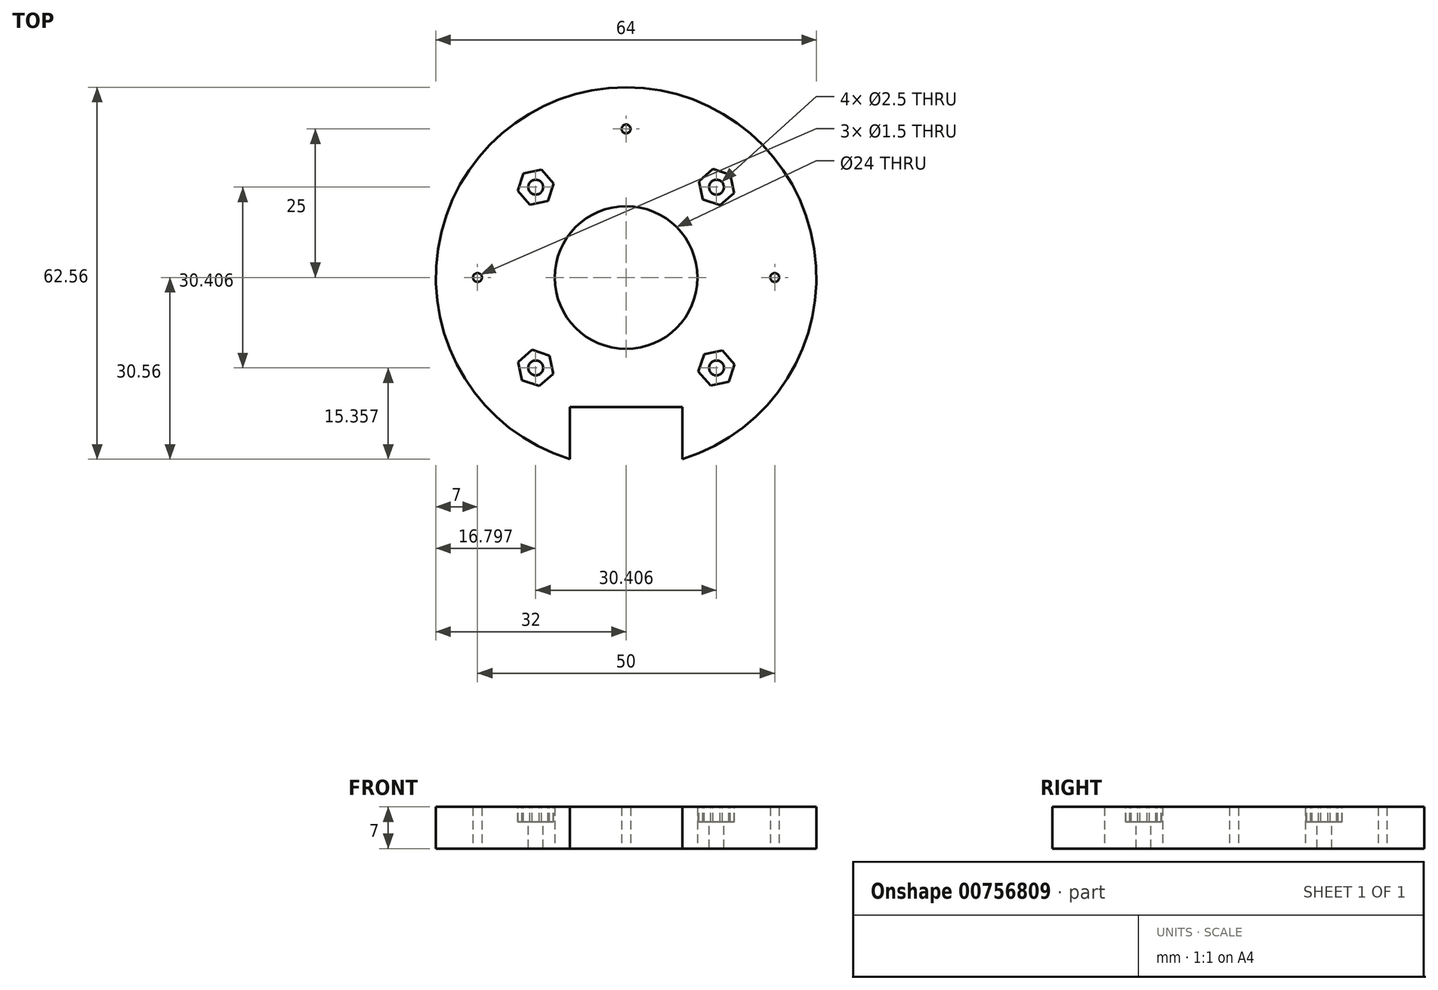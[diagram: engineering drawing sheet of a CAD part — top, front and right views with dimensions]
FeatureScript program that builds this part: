
annotation { "Feature Type Name" : "Feature", "Feature Type Description" : "" }
export const myFeature = defineFeature(function(context is Context, id is Id, definition is map)
    precondition{}
    {
        {
            var Q0;
            Q0=qCreatedBy(makeId("Top.planeOp"),FACE);
            var sketch = newSketch(context, id + "F0", { "sketchPlane" : qUnion([Q0])});
            skCircle(sketch, "E0", {"center": v(0, 0) * mm, "radius": 32 * mm});
            skCircle(sketch, "E1", {"center": v(0, 0) * mm, "radius": 12 * mm});
            skSolve(sketch);
        }
        {
            var Q0;
            Q0=makeQuery(id+"F0.imprint","IMPRINT",FACE,{"disambiguationData":[TD([[makeQuery(id+"F0.imprint","IMPRINT",EDGE,{"derivedFrom":sQuery(id+"F0.wireOp",EDGE,"E0")}),1.0]])]});
            extrude(context, id + "F1", {"entities" : qUnion([Q0]), "depth" : 7 * mm, "offsetDistance" : 25 * mm});
        }
        {
            var Q0;
            Q0=makeQuery(id+"F1.opExtrude","CAP_FACE",FACE,{"disambiguationData":[OSD([sQuery(id+"F0.wireOp",EDGE,"E0"),sQuery(id+"F0.wireOp",EDGE,"E1")])],"isStart":false});
            var sketch = newSketch(context, id + "F2", { "sketchPlane" : qUnion([Q0])});
            skLineSegment(sketch, "E2", {"start": v(-31.73, 31.73) * mm, "end": v(0, 0) * mm, "construction": true});
            skCircle(sketch, "E3", {"center": v(0, 0) * mm, "radius": 21.5 * mm, "construction": true});
            skPoint(sketch, "E4", {"position": v(-15.2, 15.2) * mm});
            skPoint(sketch, "E5.1.0", {"position": v(-15.2, -15.2) * mm});
            skPoint(sketch, "E5.2.0", {"position": v(15.2, -15.2) * mm});
            skPoint(sketch, "E5.3.0", {"position": v(15.2, 15.2) * mm});
            skCircle(sketch, "E6.cCircle", {"center": v(-15.2, 15.2) * mm, "radius": 2.7 * mm, "construction": true});
            skLineSegment(sketch, "E6.0", {"start": v(-14.21, 18.15) * mm, "end": v(-12.16, 15.82) * mm});
            skLineSegment(sketch, "E6.1", {"start": v(-12.16, 15.82) * mm, "end": v(-13.15, 12.87) * mm});
            skLineSegment(sketch, "E6.2", {"start": v(-13.15, 12.87) * mm, "end": v(-16.2, 12.26) * mm});
            skLineSegment(sketch, "E6.3", {"start": v(-16.2, 12.26) * mm, "end": v(-18.25, 14.59) * mm});
            skLineSegment(sketch, "E6.4", {"start": v(-18.25, 14.59) * mm, "end": v(-17.26, 17.53) * mm});
            skLineSegment(sketch, "E6.5", {"start": v(-17.26, 17.53) * mm, "end": v(-14.21, 18.15) * mm});
            skPoint(sketch, "E6.0.midPoint", {"position": v(-13.19, 16.98) * mm});
            skLineSegment(sketch, "E7.1.0", {"start": v(-12.87, -13.15) * mm, "end": v(-12.26, -16.2) * mm});
            skLineSegment(sketch, "E7.1.1", {"start": v(-15.82, -12.16) * mm, "end": v(-12.87, -13.15) * mm});
            skLineSegment(sketch, "E7.1.2", {"start": v(-18.15, -14.21) * mm, "end": v(-15.82, -12.16) * mm});
            skLineSegment(sketch, "E7.1.3", {"start": v(-17.53, -17.26) * mm, "end": v(-18.15, -14.21) * mm});
            skLineSegment(sketch, "E7.1.4", {"start": v(-14.59, -18.25) * mm, "end": v(-17.53, -17.26) * mm});
            skLineSegment(sketch, "E7.1.5", {"start": v(-12.26, -16.2) * mm, "end": v(-14.59, -18.25) * mm});
            skLineSegment(sketch, "E7.2.0", {"start": v(13.15, -12.87) * mm, "end": v(16.2, -12.26) * mm});
            skLineSegment(sketch, "E7.2.1", {"start": v(12.16, -15.82) * mm, "end": v(13.15, -12.87) * mm});
            skLineSegment(sketch, "E7.2.2", {"start": v(14.21, -18.15) * mm, "end": v(12.16, -15.82) * mm});
            skLineSegment(sketch, "E7.2.3", {"start": v(17.26, -17.53) * mm, "end": v(14.21, -18.15) * mm});
            skLineSegment(sketch, "E7.2.4", {"start": v(18.25, -14.59) * mm, "end": v(17.26, -17.53) * mm});
            skLineSegment(sketch, "E7.2.5", {"start": v(16.2, -12.26) * mm, "end": v(18.25, -14.59) * mm});
            skLineSegment(sketch, "E7.3.0", {"start": v(12.87, 13.15) * mm, "end": v(12.26, 16.2) * mm});
            skLineSegment(sketch, "E7.3.1", {"start": v(15.82, 12.16) * mm, "end": v(12.87, 13.15) * mm});
            skLineSegment(sketch, "E7.3.2", {"start": v(18.15, 14.21) * mm, "end": v(15.82, 12.16) * mm});
            skLineSegment(sketch, "E7.3.3", {"start": v(17.53, 17.26) * mm, "end": v(18.15, 14.21) * mm});
            skLineSegment(sketch, "E7.3.4", {"start": v(14.59, 18.25) * mm, "end": v(17.53, 17.26) * mm});
            skLineSegment(sketch, "E7.3.5", {"start": v(12.26, 16.2) * mm, "end": v(14.59, 18.25) * mm});
            skSolve(sketch);
        }
        {
            var Q0;
            Q0=sQuery(id+"F2.wireOp",VERTEX,"E4");
            var Q1;
            Q1=sQuery(id+"F2.wireOp",VERTEX,"E5.3.0");
            var Q2;
            Q2=sQuery(id+"F2.wireOp",VERTEX,"E5.2.0");
            var Q3;
            Q3=sQuery(id+"F2.wireOp",VERTEX,"E5.1.0");
            var Q4;
            Q4=makeQuery(id+"F1.opExtrude","SWEPT_BODY",BODY,{"disambiguationData":[OSD([sQuery(id+"F0.wireOp",EDGE,"E0"),sQuery(id+"F0.wireOp",EDGE,"E1")])]});
            hole(context, id + "F3", {"style" : HoleStyle.SIMPLE, "endStyle" : HoleEndStyle.THROUGH, "holeDiameter" : 2.5 * mm, "majorDiameter" : 5 * mm, "tappedDepth" : 12 * mm, "tapClearance" : 3, "startFromSketch" : true, "locations" : qUnion([Q0, Q1, Q2, Q3]), "scope" : qUnion([Q4])});
        }
        {
            var Q0;
            Q0=makeQuery(id+"F2.imprint","IMPRINT",FACE,{"disambiguationData":[TD([[makeQuery(id+"F2.imprint","IMPRINT",EDGE,{"derivedFrom":sQuery(id+"F2.wireOp",EDGE,"E6.0")}),-1.0]])]});
            var Q1;
            Q1=makeQuery(id+"F2.imprint","IMPRINT",FACE,{"disambiguationData":[TD([[makeQuery(id+"F2.imprint","IMPRINT",EDGE,{"derivedFrom":sQuery(id+"F2.wireOp",EDGE,"E7.3.0")}),-1.0]])]});
            var Q2;
            Q2=makeQuery(id+"F2.imprint","IMPRINT",FACE,{"disambiguationData":[TD([[makeQuery(id+"F2.imprint","IMPRINT",EDGE,{"derivedFrom":sQuery(id+"F2.wireOp",EDGE,"E7.2.0")}),-1.0]])]});
            var Q3;
            Q3=makeQuery(id+"F2.imprint","IMPRINT",FACE,{"disambiguationData":[TD([[makeQuery(id+"F2.imprint","IMPRINT",EDGE,{"derivedFrom":sQuery(id+"F2.wireOp",EDGE,"E7.1.0")}),-1.0]])]});
            extrude(context, id + "F4", {"entities" : qUnion([Q0, Q1, Q2, Q3]), "operationType" : NewBodyOperationType.REMOVE, "oppositeDirection" : true, "depth" : 2.5 * mm, "offsetDistance" : 25 * mm});
        }
        {
            var Q0;
            Q0=qCreatedBy(makeId("Top.planeOp"),FACE);
            var sketch = newSketch(context, id + "F5", { "sketchPlane" : qUnion([Q0])});
            skCircle(sketch, "E8", {"center": v(0, 0) * mm, "radius": 25 * mm, "construction": true});
            skCircle(sketch, "E9", {"center": v(-25, 0) * mm, "radius": 0.75 * mm});
            skCircle(sketch, "E10.1.0", {"center": v(0, -25) * mm, "radius": 0.75 * mm});
            skCircle(sketch, "E10.2.0", {"center": v(25, 0) * mm, "radius": 0.75 * mm});
            skCircle(sketch, "E10.3.0", {"center": v(0, 25) * mm, "radius": 0.75 * mm});
            skSolve(sketch);
        }
        {
            var Q0;
            Q0 = qSketchRegion(id + "F5", true);
            extrude(context, id + "F6", {"entities" : qUnion([Q0]), "operationType" : NewBodyOperationType.REMOVE, "depth" : 25 * mm, "offsetDistance" : 25 * mm});
        }
        {
            var Q0;
            Q0=qCreatedBy(makeId("Top.planeOp"),FACE);
            var sketch = newSketch(context, id + "F7", { "sketchPlane" : qUnion([Q0])});
            skLineSegment(sketch, "E11.bottom", {"start": v(9.48, -21.8) * mm, "end": v(-9.48, -21.8) * mm});
            skLineSegment(sketch, "E11.top", {"start": v(9.48, -42.2) * mm, "end": v(-9.48, -42.2) * mm});
            skLineSegment(sketch, "E11.left", {"start": v(9.48, -21.8) * mm, "end": v(9.48, -42.2) * mm});
            skLineSegment(sketch, "E11.right", {"start": v(-9.48, -21.8) * mm, "end": v(-9.48, -42.2) * mm});
            skPoint(sketch, "E11.middle", {"position": v(0, -32) * mm});
            skSolve(sketch);
        }
        {
            var Q0;
            Q0 = qSketchRegion(id + "F7", true);
            extrude(context, id + "F8", {"entities" : qUnion([Q0]), "operationType" : NewBodyOperationType.REMOVE, "depth" : 25 * mm, "offsetDistance" : 25 * mm});
        }
    });
